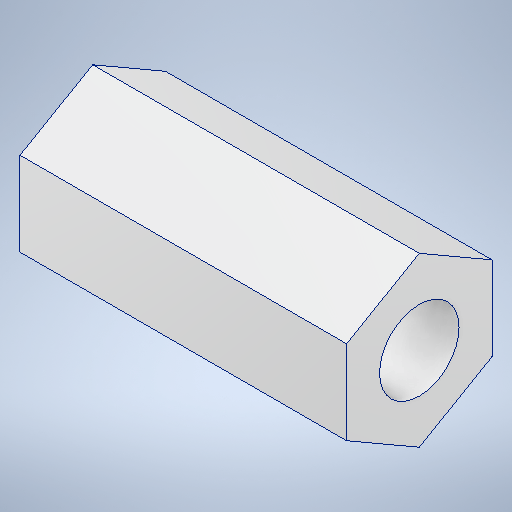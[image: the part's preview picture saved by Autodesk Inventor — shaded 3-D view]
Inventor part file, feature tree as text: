
AUTODESK INVENTOR PART (.ipt)
format: ipt  version: 2025.1 (Build 291241020, 241B)  size: 212,992 bytes
history: native  units: in
note: dims shown in document units (in); Inventor stores cm internally (conversion verified against a paired STEP export)
features: extrude x1, sketch x1
ambient origin geometry x8: Origin, YZ Plane, XZ Plane, XY Plane, X Axis, Y Axis, Z Axis, Center Point
bodies: Solid1 (feature_tree)
feature tree (2):
  extrude  "Extrusion1"  Depth=0.5in
  sketch  "Sketch1"  dims[d0=0.2732in d1=0.5in d3=1.123in d4=0.0in]
